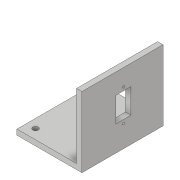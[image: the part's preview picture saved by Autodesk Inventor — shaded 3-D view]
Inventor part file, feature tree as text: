
AUTODESK INVENTOR PART (.ipt)
format: ipt  version: 2019 (Build 230136000, 136)  size: 105,472 bytes
history: native  units: in
note: dims shown in document units (in); Inventor stores cm internally (conversion verified against a paired STEP export)
features: sketch x5, extrude x4
ambient origin geometry x8: Origin, YZ Plane, XZ Plane, XY Plane, X Axis, Y Axis, Z Axis, Center Point
bodies: Solid1 (feature_tree)
feature tree (9):
  sketch  "Sketch1"  dims[d4=2.9528in d5=0.0in d6=0.1969in]
  extrude  "Extrusion1"  Depth=0.1969in
  extrude  "Extrusion2"  Depth=2.9528in TaperAngle=0.0deg
  extrude  "Extrusion3"  Depth=2.9528in TaperAngle=0.0deg
  extrude  "Extrusion4"  [1 undecoded]
  sketch  "Sketch2"  dims[d7=0.1969in d8=2.9528in d9=0.0in]
  sketch  "Sketch3"  dims[d12=2.9528in d13=0.0in d21=2.9528in d22=0.0in]
  sketch  "Sketch4"
  sketch  "Sketch5"
note: 1 required parameter value undecoded (feature->parameter linkage not recoverable at this tier; creation-order binding heuristic only, values carry confidence <= 0.55)
